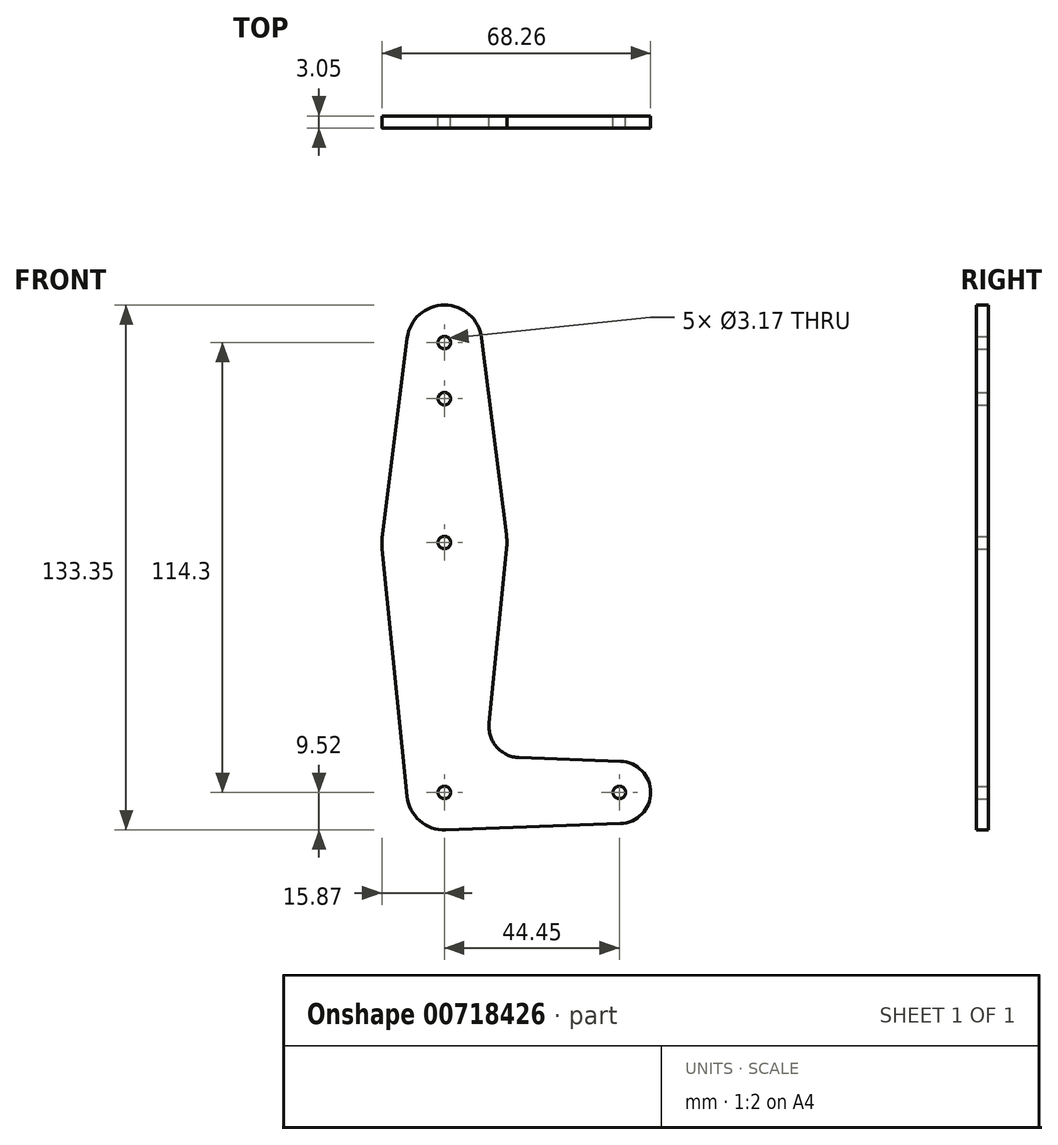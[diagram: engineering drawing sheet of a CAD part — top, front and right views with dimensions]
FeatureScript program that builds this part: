
annotation { "Feature Type Name" : "Feature", "Feature Type Description" : "" }
export const myFeature = defineFeature(function(context is Context, id is Id, definition is map)
    precondition{}
    {
        {
            var Q0;
            Q0=qCreatedBy(makeId("Front.planeOp"),FACE);
            var sketch = newSketch(context, id + "F0", { "sketchPlane" : qUnion([Q0])});
            skCircle(sketch, "E0", {"center": v(0, 0) * mm, "radius": 9.53 * mm});
            skLineSegment(sketch, "E1", {"start": v(0, 0) * mm, "end": v(0, 114.3) * mm});
            skLineSegment(sketch, "E2", {"start": v(0, 0) * mm, "end": v(44.45, 0) * mm});
            skCircle(sketch, "E3", {"center": v(44.45, 0) * mm, "radius": 7.94 * mm});
            skCircle(sketch, "E4", {"center": v(0, 114.3) * mm, "radius": 9.53 * mm});
            skCircle(sketch, "E5", {"center": v(0, 63.5) * mm, "radius": 15.88 * mm});
            skLineSegment(sketch, "E6", {"start": v(9.45, 115.5) * mm, "end": v(15.75, 65.48) * mm});
            skLineSegment(sketch, "E7", {"start": v(-9.45, 115.5) * mm, "end": v(-15.75, 65.48) * mm});
            skLineSegment(sketch, "E8", {"start": v(-15.83, 62.3) * mm, "end": v(-15.8, 61.91) * mm});
            skLineSegment(sketch, "E9", {"start": v(15.8, 61.91) * mm, "end": v(11.34, 17.6) * mm});
            skLineSegment(sketch, "E10", {"start": v(44.73, -7.93) * mm, "end": v(0, -9.53) * mm});
            skLineSegment(sketch, "E11", {"start": v(44.73, 7.93) * mm, "end": v(18.97, 8.85) * mm});
            skPoint(sketch, "E12.visualSharp", {"position": v(10.5, 9.16) * mm});
            skArc(sketch, "E12.filletArc", {"start": v(11.34, 17.6) * mm, "mid": v(13.26, 11.57) * mm, "end": v(18.97, 8.85) * mm});
            skCircle(sketch, "E13", {"center": v(0, 114.3) * mm, "radius": 1.59 * mm});
            skCircle(sketch, "E14", {"center": v(0, 63.5) * mm, "radius": 1.59 * mm});
            skCircle(sketch, "E15", {"center": v(0, 0) * mm, "radius": 1.59 * mm});
            skCircle(sketch, "E16", {"center": v(44.45, 0) * mm, "radius": 1.59 * mm});
            skCircle(sketch, "E17", {"center": v(0, 100.03) * mm, "radius": 1.59 * mm});
            skPoint(sketch, "E18.orphan", {"position": v(-9.57, 0) * mm});
            skLineSegment(sketch, "E19", {"start": v(-15.8, 61.91) * mm, "end": v(-9.48, -0.95) * mm});
            skSolve(sketch);
        }
        {
            var Q0;
            Q0 = qSketchRegion(id + "F0", true);
            var Q1;
            {var subQ0=sQuery(id+"F0.wireOp",EDGE,"E1");var subQ1=sQuery(id+"F0.wireOp",EDGE,"E0");var subQ2=makeQuery(id+"F0.imprint","INTERSECT",VERTEX,{"derivedFrom":[subQ1,subQ0]});Q1=makeQuery(id+"F0.imprint","IMPRINT",FACE,{"disambiguationData":[TD([[makeQuery(id+"F0.imprint","IMPRINT",EDGE,{"disambiguationData":[TD([[subQ2,1.0]])],"derivedFrom":subQ1}),1.0]])]});}
            extrude(context, id + "F1", {"entities" : qUnion([Q0, Q1]), "depth" : 3.05 * mm, "offsetDistance" : 25.4 * mm});
        }
    });
